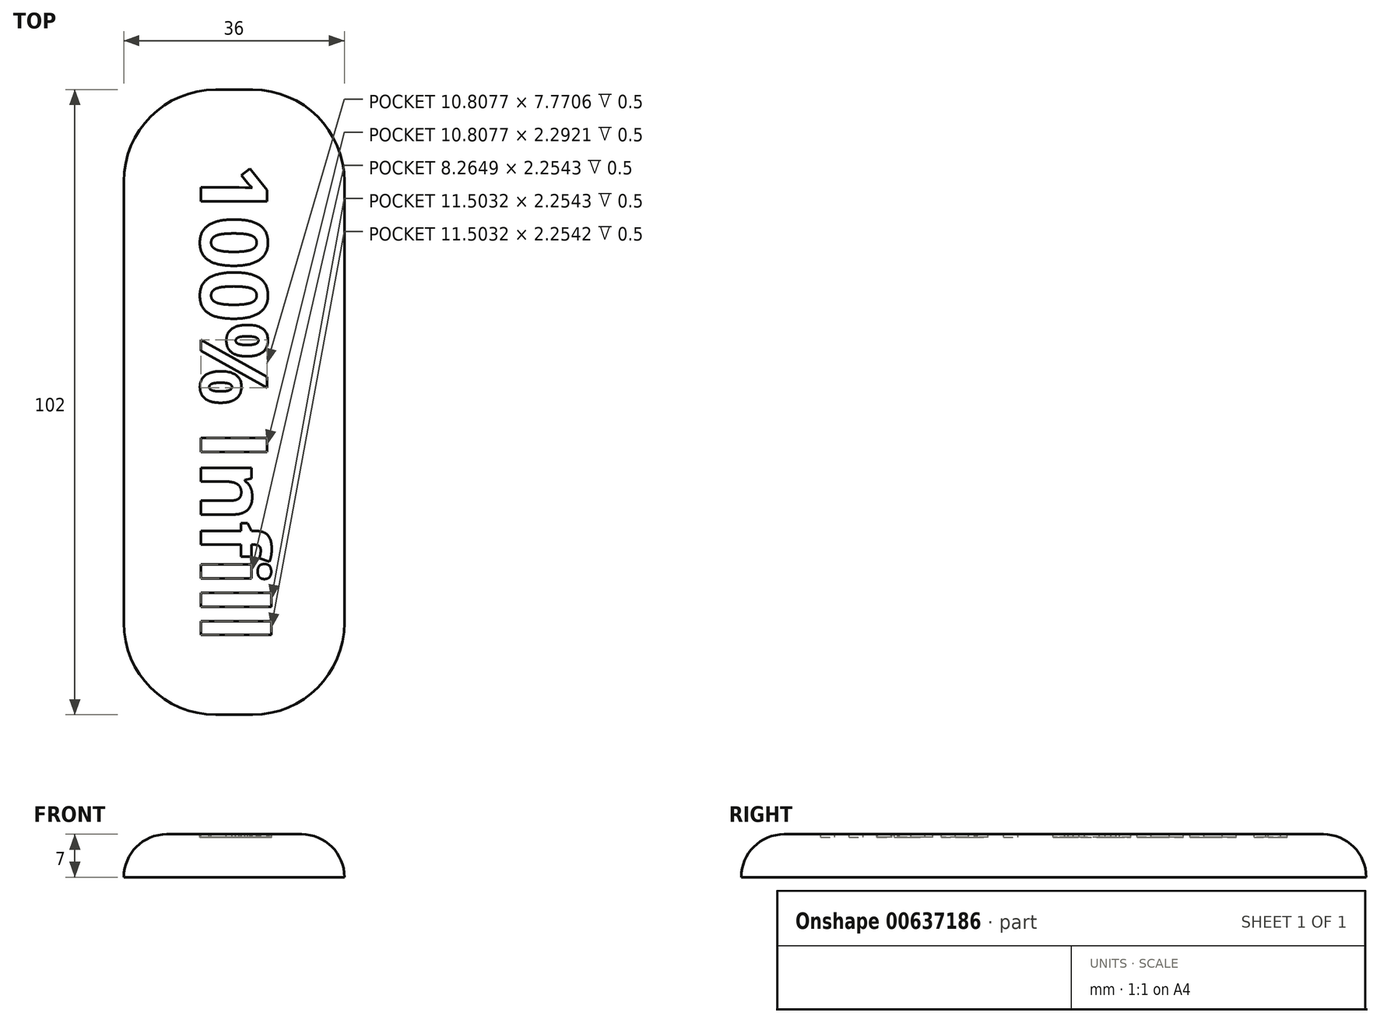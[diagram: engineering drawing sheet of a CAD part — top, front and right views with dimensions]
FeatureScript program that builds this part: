
annotation { "Feature Type Name" : "Feature", "Feature Type Description" : "" }
export const myFeature = defineFeature(function(context is Context, id is Id, definition is map)
    precondition{}
    {
        {
            var Q0;
            Q0=qCreatedBy(makeId("Top.planeOp"),FACE);
            var sketch = newSketch(context, id + "F0", { "sketchPlane" : qUnion([Q0])});
            skLineSegment(sketch, "E0.bottom", {"start": v(18, -51) * mm, "end": v(-18, -51) * mm});
            skLineSegment(sketch, "E0.top", {"start": v(18, 51) * mm, "end": v(-18, 51) * mm});
            skLineSegment(sketch, "E0.left", {"start": v(18, -51) * mm, "end": v(18, 51) * mm});
            skLineSegment(sketch, "E0.right", {"start": v(-18, -51) * mm, "end": v(-18, 51) * mm});
            skPoint(sketch, "E0.middle", {"position": v(0, 0) * mm});
            skSolve(sketch);
        }
        {
            var Q0;
            Q0 = qSketchRegion(id + "F0", true);
            extrude(context, id + "F1", {"entities" : qUnion([Q0]), "endBound" : BoundingType.SYMMETRIC, "depth" : 7 * mm, "offsetDistance" : 25 * mm});
        }
        {
            var Q0;
            Q0=makeQuery(id+"F1.opExtrude","SWEPT_EDGE",EDGE,{"disambiguationData":[OSD([sQuery(id+"F0.wireOp",EDGE,"E0.bottom"),sQuery(id+"F0.wireOp",EDGE,"E0.right")])]});
            var Q1;
            Q1=makeQuery(id+"F1.opExtrude","SWEPT_EDGE",EDGE,{"disambiguationData":[OSD([sQuery(id+"F0.wireOp",EDGE,"E0.bottom"),sQuery(id+"F0.wireOp",EDGE,"E0.left")])]});
            var Q2;
            Q2=makeQuery(id+"F1.opExtrude","SWEPT_EDGE",EDGE,{"disambiguationData":[OSD([sQuery(id+"F0.wireOp",EDGE,"E0.top"),sQuery(id+"F0.wireOp",EDGE,"E0.left")])]});
            var Q3;
            Q3=makeQuery(id+"F1.opExtrude","SWEPT_EDGE",EDGE,{"disambiguationData":[OSD([sQuery(id+"F0.wireOp",EDGE,"E0.top"),sQuery(id+"F0.wireOp",EDGE,"E0.right")])]});
            fillet(context, id + "F2", {"entities" : qUnion([Q0, Q1, Q2, Q3]), "radius" : 15 * mm, "tangentPropagation" : true, "allowEdgeOverflow" : false});
        }
        {
            var Q0;
            Q0=makeQuery(id+"F1.opExtrude","CAP_FACE",FACE,{"disambiguationData":[OSD([sQuery(id+"F0.wireOp",EDGE,"E0.bottom"),sQuery(id+"F0.wireOp",EDGE,"E0.top"),sQuery(id+"F0.wireOp",EDGE,"E0.left"),sQuery(id+"F0.wireOp",EDGE,"E0.right")])],"isStart":false});
            fillet(context, id + "F3", {"entities" : qUnion([Q0]), "radius" : 7 * mm, "tangentPropagation" : true, "allowEdgeOverflow" : false});
        }
        {
            var Q0;
            Q0=makeQuery(id+"F1.opExtrude","CAP_FACE",FACE,{"disambiguationData":[OSD([sQuery(id+"F0.wireOp",EDGE,"E0.bottom"),sQuery(id+"F0.wireOp",EDGE,"E0.top"),sQuery(id+"F0.wireOp",EDGE,"E0.left"),sQuery(id+"F0.wireOp",EDGE,"E0.right")])],"isStart":false});
            var sketch = newSketch(context, id + "F4", { "sketchPlane" : qUnion([Q0])});
            skText(sketch, "E1", { "text": "100% Infill", "fontName": "OpenSans-Bold.ttf"});
            skLineSegment(sketch, "E2", {"start": v(0, 39) * mm, "end": v(0, -39) * mm, "construction": true});
            const initialGuessF4  = {"E1": [-0.00545, 0.039, 0, -1, 0.0109]};
            skSetInitialGuess(sketch, initialGuessF4);
            skSolve(sketch);
        }
        {
            var Q0;
            Q0 = qSketchRegion(id + "F4", true);
            extrude(context, id + "F5", {"entities" : qUnion([Q0]), "operationType" : NewBodyOperationType.REMOVE, "oppositeDirection" : true, "depth" : 0.5 * mm, "offsetDistance" : 25 * mm});
        }
    });
